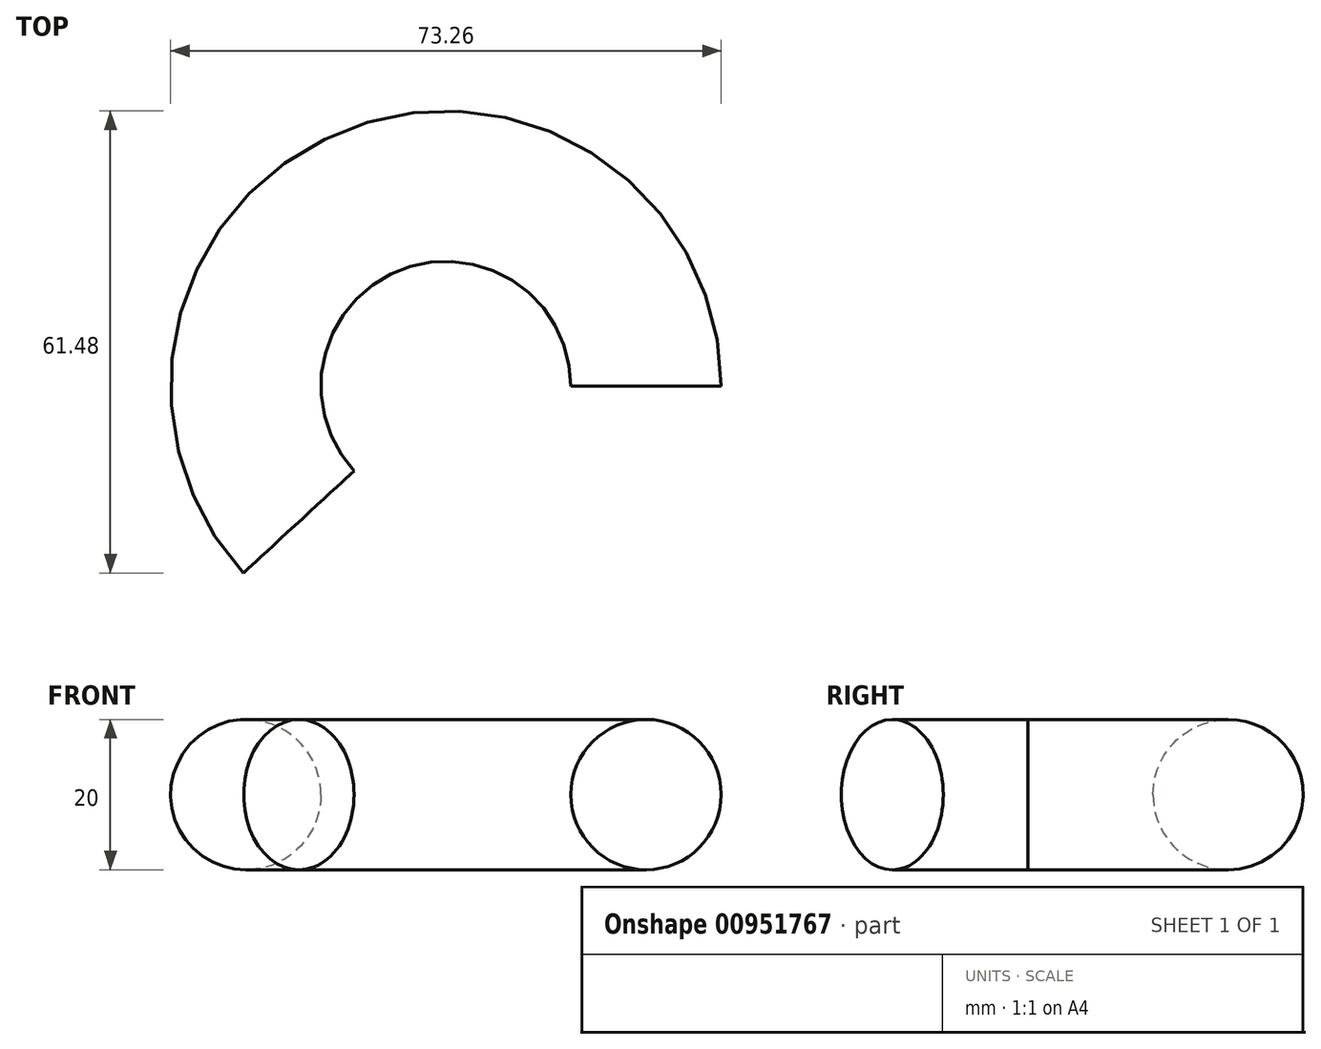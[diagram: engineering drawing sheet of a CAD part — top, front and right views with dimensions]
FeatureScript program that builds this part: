
annotation { "Feature Type Name" : "Feature", "Feature Type Description" : "" }
export const myFeature = defineFeature(function(context is Context, id is Id, definition is map)
    precondition{}
    {
        {
            var Q0;
            Q0=qCreatedBy(makeId("Top.planeOp"),FACE);
            var sketch = newSketch(context, id + "F0", { "sketchPlane" : qUnion([Q0])});
            skArc(sketch, "E0", {"start": v(40, 0) * mm, "mid": v(-14.57, 37.25) * mm, "end": v(-29.4, -27.13) * mm});
            skSolve(sketch);
        }
        {
            var Q0;
            Q0=sQuery(id+"F0.wireOp",VERTEX,"E0.start");
            var Q1;
            Q1=sQuery(id+"F0.wireOp",EDGE,"E0");
            cPlane(context, id + "F1", {"entities" : qUnion([Q0, Q1]), "cplaneType" : CPlaneType.CURVE_POINT, "offset" : 25 * mm, "width" : 150 * mm, "height" : 150 * mm});
        }
        {
            var Q0;
            Q0=qCreatedBy(id+"F1.planeOp",FACE);
            var sketch = newSketch(context, id + "F2", { "sketchPlane" : qUnion([Q0])});
            skCircle(sketch, "E1", {"center": v(-26.63, 0) * mm, "radius": 10 * mm});
            skSolve(sketch);
        }
        {
            var Q0;
            Q0=makeQuery(id+"F2.imprint","IMPRINT",FACE,{"disambiguationData":[TD([[makeQuery(id+"F2.imprint","IMPRINT",EDGE,{"derivedFrom":sQuery(id+"F2.wireOp",EDGE,"E1")}),1.0]])]});
            var Q1;
            Q1=sQuery(id+"F0.wireOp",EDGE,"E0");
            sweep(context, id + "F3", {"profiles" : qUnion([Q0]), "path" : qUnion([Q1])});
        }
    });
